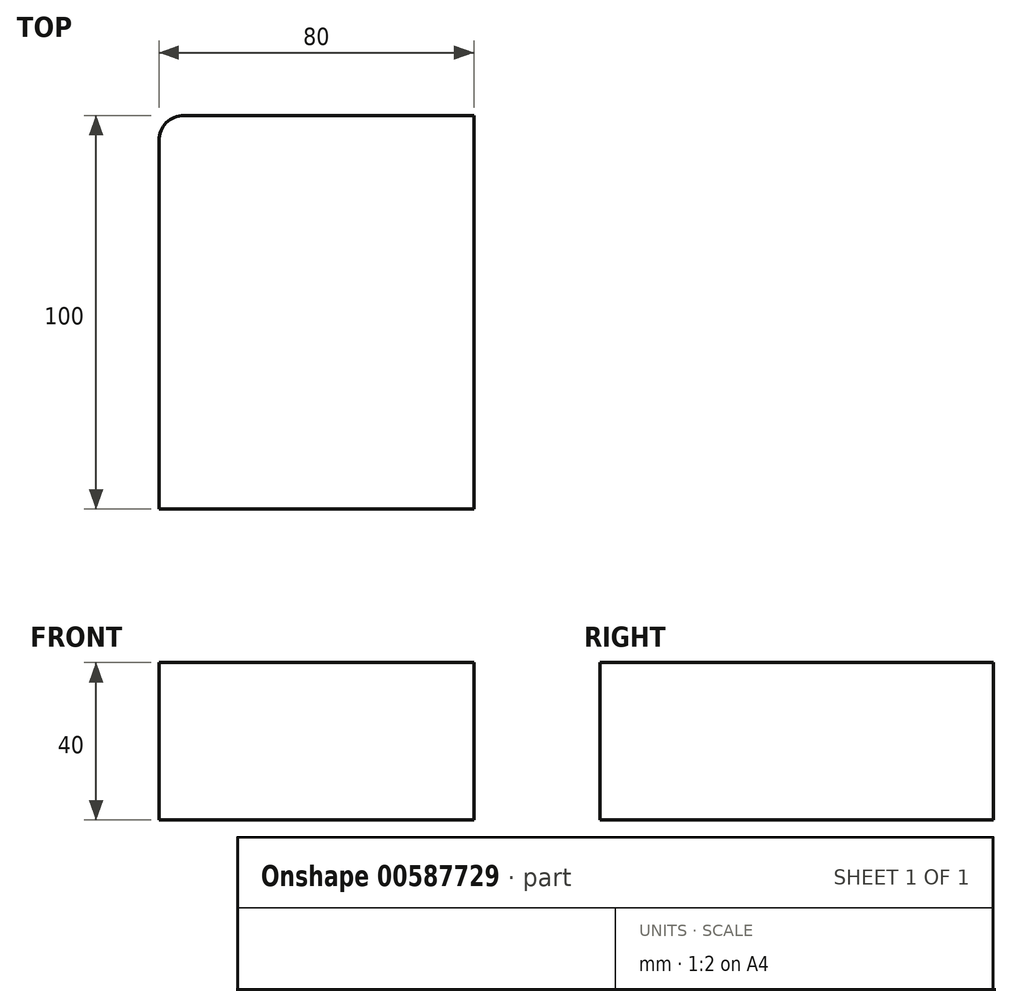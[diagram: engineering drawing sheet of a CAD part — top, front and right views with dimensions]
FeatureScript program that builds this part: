
annotation { "Feature Type Name" : "Feature", "Feature Type Description" : "" }
export const myFeature = defineFeature(function(context is Context, id is Id, definition is map)
    precondition{}
    {
        {
            var Q0;
            Q0=qCreatedBy(makeId("Top.planeOp"),FACE);
            var sketch = newSketch(context, id + "F0", { "sketchPlane" : qUnion([Q0])});
            skLineSegment(sketch, "E0.bottom", {"start": v(6.35, 0) * mm, "end": v(80, 0) * mm});
            skLineSegment(sketch, "E0.top", {"start": v(0, -100) * mm, "end": v(80, -100) * mm});
            skLineSegment(sketch, "E0.left", {"start": v(0, -6.35) * mm, "end": v(0, -100) * mm});
            skLineSegment(sketch, "E0.right", {"start": v(80, 0) * mm, "end": v(80, -100) * mm});
            skPoint(sketch, "E1.visualSharp", {"position": v(0, 0) * mm});
            skArc(sketch, "E1.filletArc", {"start": v(6.35, 0) * mm, "mid": v(1.86, -1.86) * mm, "end": v(0, -6.35) * mm});
            skSolve(sketch);
        }
        {
            var Q0;
            Q0 = qSketchRegion(id + "F0", true);
            extrude(context, id + "F1", {"entities" : qUnion([Q0]), "oppositeDirection" : true, "depth" : 40 * mm, "offsetDistance" : 25 * mm});
        }
    });
